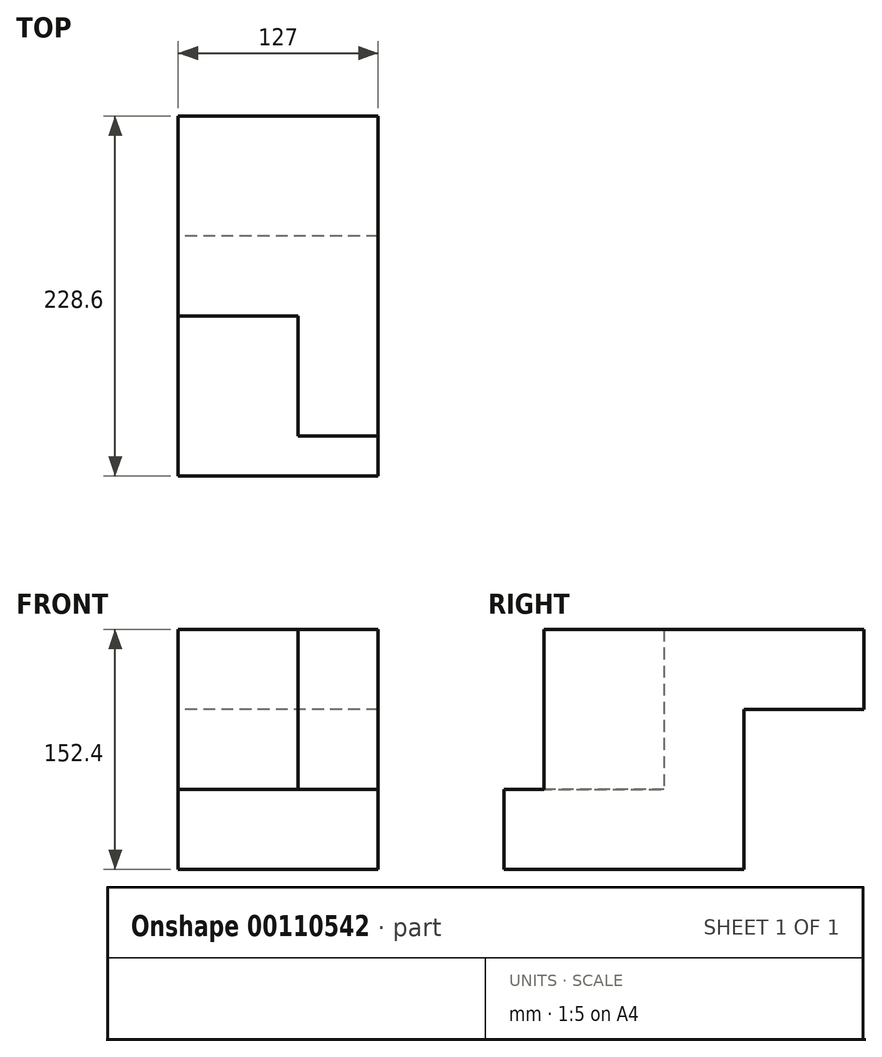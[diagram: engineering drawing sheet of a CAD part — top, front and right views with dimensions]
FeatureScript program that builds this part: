
annotation { "Feature Type Name" : "Feature", "Feature Type Description" : "" }
export const myFeature = defineFeature(function(context is Context, id is Id, definition is map)
    precondition{}
    {
        {
            var Q0;
            Q0=qCreatedBy(makeId("Front.planeOp"),FACE);
            var sketch = newSketch(context, id + "F0", { "sketchPlane" : qUnion([Q0])});
            skLineSegment(sketch, "E0", {"start": v(-59.45, 83.96) * mm, "end": v(-59.45, -68.44) * mm});
            skLineSegment(sketch, "E1", {"start": v(-59.45, -68.44) * mm, "end": v(67.55, -68.44) * mm});
            skLineSegment(sketch, "E2", {"start": v(67.55, -68.44) * mm, "end": v(67.55, 83.96) * mm});
            skLineSegment(sketch, "E3", {"start": v(67.55, 83.96) * mm, "end": v(-59.45, 83.96) * mm});
            skSolve(sketch);
        }
        {
            var Q0;
            Q0 = qSketchRegion(id + "F0", true);
            extrude(context, id + "F1", {"entities" : qUnion([Q0]), "depth" : 50.8 * mm});
        }
        {
            var Q0;
            Q0=makeQuery(id+"F1.opExtrude","CAP_FACE",FACE,{"disambiguationData":[OSD([sQuery(id+"F0.wireOp",EDGE,"E0"),sQuery(id+"F0.wireOp",EDGE,"E1"),sQuery(id+"F0.wireOp",EDGE,"E2"),sQuery(id+"F0.wireOp",EDGE,"E3")])],"isStart":true});
            var sketch = newSketch(context, id + "F2", { "sketchPlane" : qUnion([Q0])});
            skLineSegment(sketch, "E4", {"start": v(-67.55, 33.16) * mm, "end": v(59.45, 33.16) * mm});
            skLineSegment(sketch, "E5", {"start": v(59.45, 33.16) * mm, "end": v(59.45, 83.96) * mm});
            skLineSegment(sketch, "E6", {"start": v(59.45, 83.96) * mm, "end": v(-67.55, 83.96) * mm});
            skLineSegment(sketch, "E7", {"start": v(-67.55, 83.96) * mm, "end": v(-67.55, 33.16) * mm});
            skSolve(sketch);
        }
        {
            var Q0;
            Q0 = qSketchRegion(id + "F2", true);
            extrude(context, id + "F3", {"entities" : qUnion([Q0]), "operationType" : NewBodyOperationType.ADD, "depth" : 76.2 * mm});
        }
        {
            var Q0;
            Q0=makeQuery(id+"F1.opExtrude","CAP_FACE",FACE,{"disambiguationData":[OSD([sQuery(id+"F0.wireOp",EDGE,"E0"),sQuery(id+"F0.wireOp",EDGE,"E1"),sQuery(id+"F0.wireOp",EDGE,"E2"),sQuery(id+"F0.wireOp",EDGE,"E3")])],"isStart":false});
            var sketch = newSketch(context, id + "F4", { "sketchPlane" : qUnion([Q0])});
            skLineSegment(sketch, "E8", {"start": v(-59.45, -17.64) * mm, "end": v(67.55, -17.64) * mm});
            skLineSegment(sketch, "E9", {"start": v(67.55, -17.64) * mm, "end": v(67.55, -68.44) * mm});
            skLineSegment(sketch, "E10", {"start": v(67.55, -68.44) * mm, "end": v(-59.45, -68.44) * mm});
            skLineSegment(sketch, "E11", {"start": v(-59.45, -17.64) * mm, "end": v(-59.45, -68.44) * mm});
            skSolve(sketch);
        }
        {
            var Q0;
            Q0 = qSketchRegion(id + "F4", true);
            extrude(context, id + "F5", {"entities" : qUnion([Q0]), "operationType" : NewBodyOperationType.ADD, "depth" : 101.6 * mm});
        }
        {
            var Q0;
            Q0=makeQuery(id+"F5.opExtrude","SWEPT_FACE",FACE,{"disambiguationData":[OSD([sQuery(id+"F4.wireOp",EDGE,"E8")])]});
            var sketch = newSketch(context, id + "F6", { "sketchPlane" : qUnion([Q0])});
            skLineSegment(sketch, "E12", {"start": v(16.75, -50.8) * mm, "end": v(16.75, -127) * mm});
            skLineSegment(sketch, "E13", {"start": v(16.75, -127) * mm, "end": v(67.55, -127) * mm});
            skLineSegment(sketch, "E14", {"start": v(67.55, -127) * mm, "end": v(67.55, -50.8) * mm});
            skLineSegment(sketch, "E15", {"start": v(67.55, -50.8) * mm, "end": v(16.75, -50.8) * mm});
            skSolve(sketch);
        }
        {
            var Q0;
            Q0 = qSketchRegion(id + "F6", true);
            extrude(context, id + "F7", {"entities" : qUnion([Q0]), "operationType" : NewBodyOperationType.ADD, "depth" : 101.6 * mm});
        }
    });
